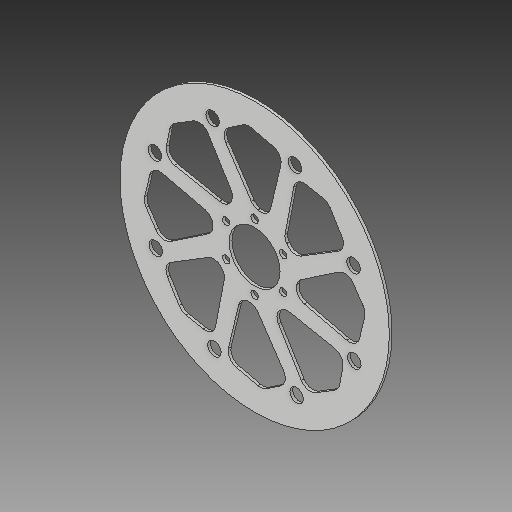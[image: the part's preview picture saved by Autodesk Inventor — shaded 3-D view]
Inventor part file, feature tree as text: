
AUTODESK INVENTOR PART (.ipt)
format: ipt  version: 2019.2 (Build 232265000, 265)  size: 210,432 bytes
history: native  units: mm
features: extrude x2, pattern_circular x2, hole x1, fillet x1, sketch x1
ambient origin geometry x8: Origin, YZ Plane, XZ Plane, XY Plane, X Axis, Y Axis, Z Axis, Center Point
bodies: Solid1 (feature_tree)
feature tree (7):
  extrude  "Extrusion1"  Depth=7.0mm
  hole  "Hole1"  [1 undecoded]
  pattern_circular  "Circular Pattern1"  [2 undecoded]
  extrude  "Extrusion2"  Depth=7.0mm TaperAngle=360.0deg
  fillet  "Fillet1"  Radius=10.0mm
  pattern_circular  "Circular Pattern2"  [2 undecoded]
  sketch  "Sketch2"  dims[d0=180.0mm d1=34.0mm d2=1.8mm d3=0.0mm d4=22.0mm d5=5.0mm d6=6.0mm d7=4.0mm d8=2.0mm d9=90.0deg d10=8.0mm d11=20.594885mm d12=60.0mm d13=360.0deg d15=10.0mm d16=0.0mm d17=7.0mm d18=80.0mm d19=360.0deg]
note: 5 required parameter values undecoded (feature->parameter linkage not recoverable at this tier; creation-order binding heuristic only, values carry confidence <= 0.55)
